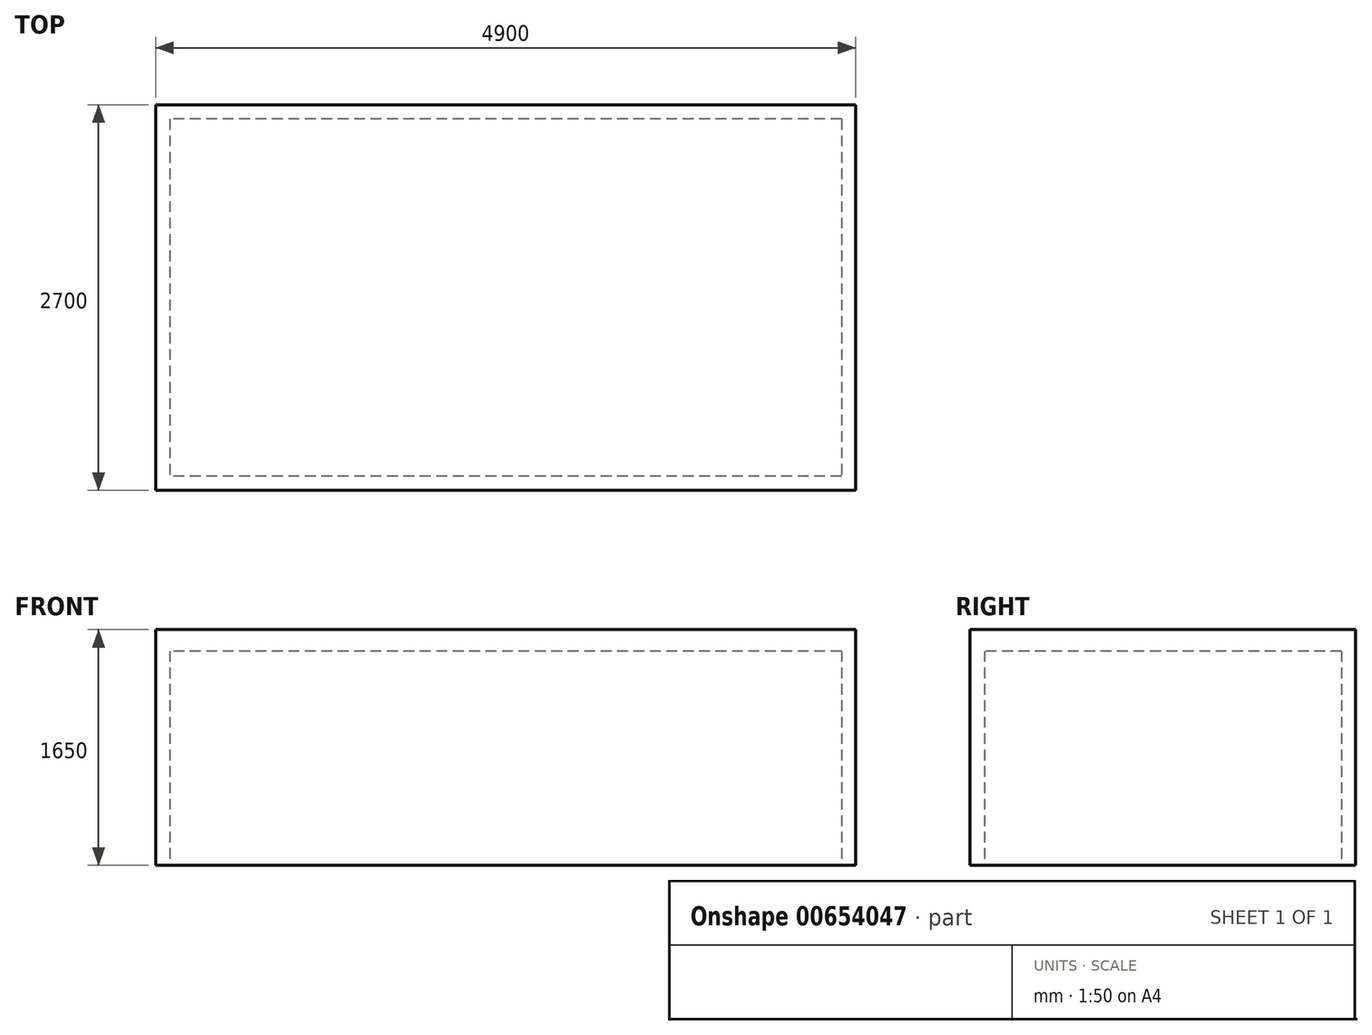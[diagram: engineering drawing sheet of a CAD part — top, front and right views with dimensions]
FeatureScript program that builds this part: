
annotation { "Feature Type Name" : "Feature", "Feature Type Description" : "" }
export const myFeature = defineFeature(function(context is Context, id is Id, definition is map)
    precondition{}
    {
        {
            var Q0;
            Q0=qCreatedBy(makeId("Top.planeOp"),FACE);
            var sketch = newSketch(context, id + "F0", { "sketchPlane" : qUnion([Q0])});
            skLineSegment(sketch, "E0.bottom", {"start": v(2350, 1250) * mm, "end": v(-2350, 1250) * mm});
            skLineSegment(sketch, "E0.top", {"start": v(2350, -1250) * mm, "end": v(-2350, -1250) * mm});
            skLineSegment(sketch, "E0.left", {"start": v(2350, 1250) * mm, "end": v(2350, -1250) * mm});
            skLineSegment(sketch, "E0.right", {"start": v(-2350, 1250) * mm, "end": v(-2350, -1250) * mm});
            skPoint(sketch, "E0.middle", {"position": v(0, 0) * mm});
            skLineSegment(sketch, "E1.bottom", {"start": v(2450, -1350) * mm, "end": v(-2450, -1350) * mm});
            skLineSegment(sketch, "E1.top", {"start": v(2450, 1350) * mm, "end": v(-2450, 1350) * mm});
            skLineSegment(sketch, "E1.left", {"start": v(2450, -1350) * mm, "end": v(2450, 1350) * mm});
            skLineSegment(sketch, "E1.right", {"start": v(-2450, -1350) * mm, "end": v(-2450, 1350) * mm});
            skSolve(sketch);
        }
        {
            var Q0;
            Q0=makeQuery(id+"F0.imprint","IMPRINT",FACE,{"disambiguationData":[TD([[makeQuery(id+"F0.imprint","IMPRINT",EDGE,{"derivedFrom":sQuery(id+"F0.wireOp",EDGE,"E0.bottom")}),-1.0]])]});
            extrude(context, id + "F1", {"entities" : qUnion([Q0]), "depth" : 1500 * mm, "offsetDistance" : 25 * mm});
        }
        {
            var Q0;
            Q0=makeQuery(id+"F1.opExtrude","CAP_FACE",FACE,{"disambiguationData":[OSD([sQuery(id+"F0.wireOp",EDGE,"E0.bottom"),sQuery(id+"F0.wireOp",EDGE,"E0.top"),sQuery(id+"F0.wireOp",EDGE,"E0.left"),sQuery(id+"F0.wireOp",EDGE,"E0.right"),sQuery(id+"F0.wireOp",EDGE,"E1.bottom"),sQuery(id+"F0.wireOp",EDGE,"E1.top"),sQuery(id+"F0.wireOp",EDGE,"E1.left"),sQuery(id+"F0.wireOp",EDGE,"E1.right")])],"isStart":false});
            var sketch = newSketch(context, id + "F2", { "sketchPlane" : qUnion([Q0])});
            skLineSegment(sketch, "E2.bottom", {"start": v(-2450, 1350) * mm, "end": v(2450, 1350) * mm});
            skLineSegment(sketch, "E2.top", {"start": v(-2450, -1350) * mm, "end": v(2450, -1350) * mm});
            skLineSegment(sketch, "E2.left", {"start": v(-2450, 1350) * mm, "end": v(-2450, -1350) * mm});
            skLineSegment(sketch, "E2.right", {"start": v(2450, 1350) * mm, "end": v(2450, -1350) * mm});
            skPoint(sketch, "E2.middle", {"position": v(0, 0) * mm});
            skSolve(sketch);
        }
        {
            var Q0;
            Q0=makeQuery(id+"F2.imprint","IMPRINT",FACE,{"disambiguationData":[TD([[makeQuery(id+"F2.imprint","IMPRINT",EDGE,{"derivedFrom":makeQuery(id+"F1.opExtrude","CAP_EDGE",EDGE,{"disambiguationData":[OSD([sQuery(id+"F0.wireOp",EDGE,"E0.bottom")])],"isStart":false})}),1.0]])]});
            var Q1;
            Q1=makeQuery(id+"F2.imprint","IMPRINT",FACE,{"disambiguationData":[TD([[makeQuery(id+"F2.imprint","IMPRINT",EDGE,{"derivedFrom":sQuery(id+"F2.wireOp",EDGE,"E2.bottom")}),1.0]])]});
            extrude(context, id + "F3", {"entities" : qUnion([Q0, Q1]), "operationType" : NewBodyOperationType.ADD, "depth" : 150 * mm, "offsetDistance" : 25 * mm});
        }
    });
